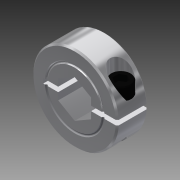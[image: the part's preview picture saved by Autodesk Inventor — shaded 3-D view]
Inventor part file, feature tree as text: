
AUTODESK INVENTOR PART (.ipt)
format: ipt  version: 2016 SP1 (Build 200210100, 210)  size: 259,584 bytes
history: native  units: in
note: dims shown in document units (in); Inventor stores cm internally (conversion verified against a paired STEP export)
features: extrude x2, sketch x2, other x1, imported_body x1
ambient origin geometry x8: Origin, YZ Plane, XZ Plane, XY Plane, X Axis, Y Axis, Z Axis, Center Point
bodies: Solid1 (feature_tree)
feature tree (6):
  other  "CL-8-A1"
  extrude  "Extrusion1"  Depth=0.4375in TaperAngle=0.0deg
  extrude  "Extrusion2"  [1 undecoded]
  imported_body  "Base1"
  sketch  "Sketch2"  dims[d0=0.5in d1=0.4375in d2=0.0in]
  sketch  "Sketch3"  dims[d3=1.0in d4=0.0in]
note: 1 required parameter value undecoded (feature->parameter linkage not recoverable at this tier; creation-order binding heuristic only, values carry confidence <= 0.55)
